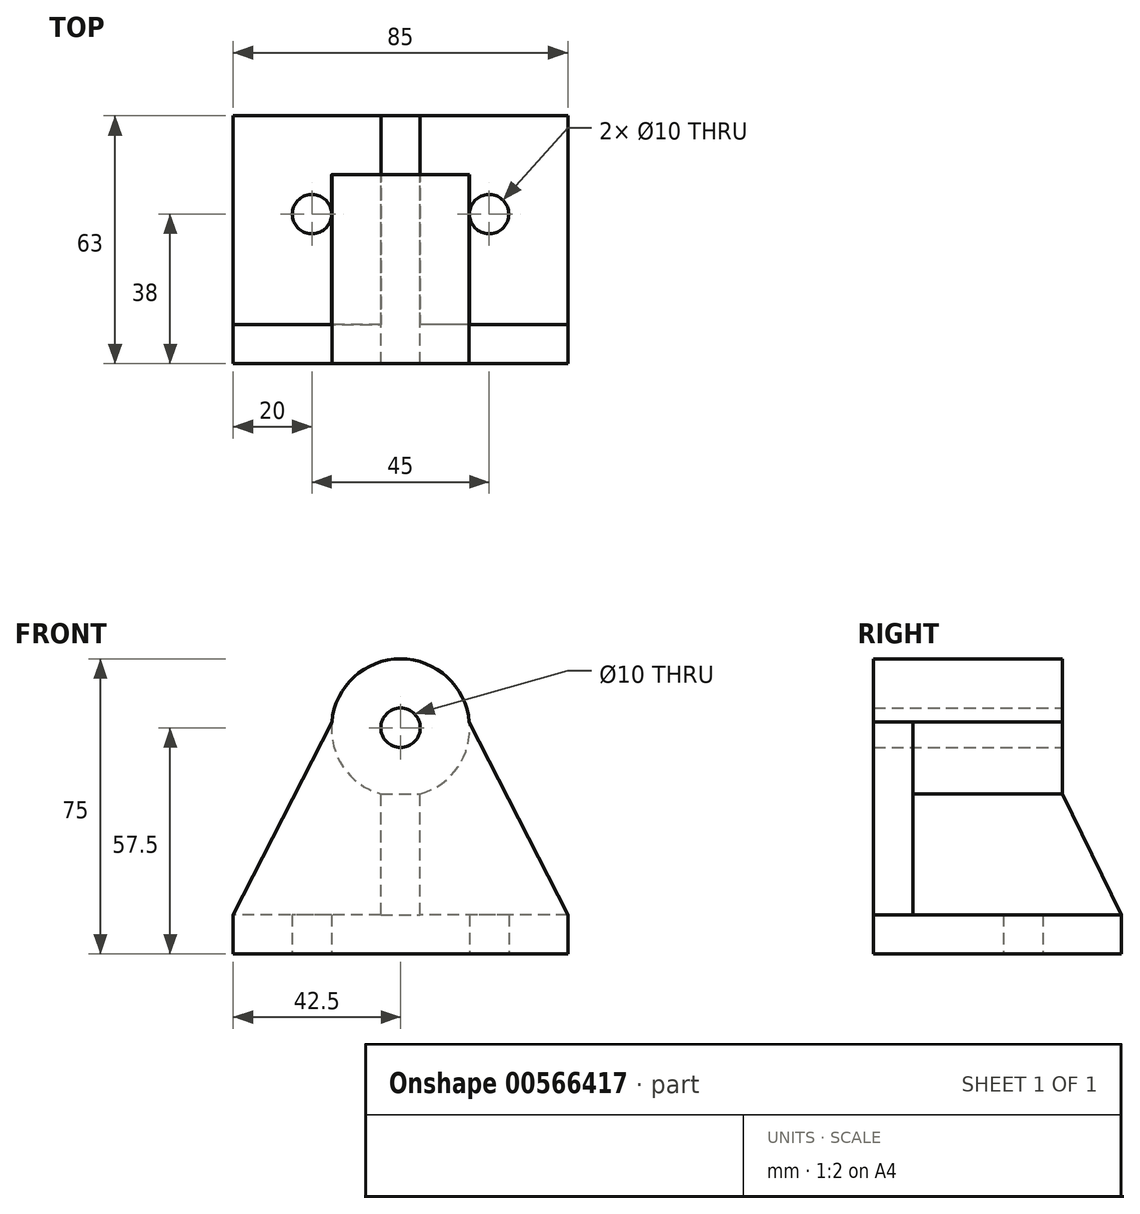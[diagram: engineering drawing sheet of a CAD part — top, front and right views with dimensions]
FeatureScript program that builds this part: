
annotation { "Feature Type Name" : "Feature", "Feature Type Description" : "" }
export const myFeature = defineFeature(function(context is Context, id is Id, definition is map)
    precondition{}
    {
        {
            var Q0;
            Q0=qCreatedBy(makeId("Front.planeOp"),FACE);
            var sketch = newSketch(context, id + "F0", { "sketchPlane" : qUnion([Q0])});
            skLineSegment(sketch, "E0", {"start": v(0, 0) * mm, "end": v(-42.5, 0) * mm});
            skLineSegment(sketch, "E1", {"start": v(-42.5, 0) * mm, "end": v(-42.5, 10) * mm});
            skCircle(sketch, "E2", {"center": v(0, 57.5) * mm, "radius": 17.5 * mm});
            skCircle(sketch, "E3", {"center": v(0, 57.5) * mm, "radius": 5 * mm});
            skLineSegment(sketch, "E4", {"start": v(0, 0) * mm, "end": v(-5, 0) * mm});
            skLineSegment(sketch, "E5", {"start": v(0, 0) * mm, "end": v(5, 0) * mm});
            skLineSegment(sketch, "E6", {"start": v(0, 0) * mm, "end": v(42.5, 0) * mm});
            skPoint(sketch, "E6.endSnap0", {"position": v(2.5, 0) * mm});
            skLineSegment(sketch, "E7", {"start": v(42.5, 0) * mm, "end": v(42.5, 10) * mm});
            skLineSegment(sketch, "E8", {"start": v(42.5, 10) * mm, "end": v(-42.5, 10) * mm});
            skLineSegment(sketch, "E9", {"start": v(17.44, 58.96) * mm, "end": v(42.5, 10) * mm});
            skLineSegment(sketch, "E10", {"start": v(-17.44, 58.96) * mm, "end": v(-42.5, 10) * mm});
            skLineSegment(sketch, "E11", {"start": v(0, 75) * mm, "end": v(0, 57.5) * mm, "construction": true});
            skLineSegment(sketch, "E12", {"start": v(-5, 0) * mm, "end": v(-5, 40.73) * mm});
            skLineSegment(sketch, "E13", {"start": v(5, 0) * mm, "end": v(5, 40.73) * mm});
            skSolve(sketch);
        }
        {
            var Q0;
            Q0 = qSketchRegion(id + "F0", true);
            extrude(context, id + "F1", {"entities" : qUnion([Q0]), "depth" : 63 * mm, "offsetDistance" : 25 * mm});
        }
        {
            var Q0;
            Q0=qCreatedBy(makeId("Top.planeOp"),FACE);
            var sketch = newSketch(context, id + "F2", { "sketchPlane" : qUnion([Q0])});
            skCircle(sketch, "E14", {"center": v(-22.5, -25) * mm, "radius": 5 * mm});
            skCircle(sketch, "E15.MirrorC", {"center": v(22.5, -25) * mm, "radius": 5 * mm});
            skSolve(sketch);
        }
        {
            var Q0;
            Q0 = qSketchRegion(id + "F2", true);
            extrude(context, id + "F3", {"entities" : qUnion([Q0]), "operationType" : NewBodyOperationType.REMOVE, "depth" : 10 * mm, "offsetDistance" : 25 * mm});
        }
        {
            var Q0;
            Q0=makeQuery(id+"F1.opExtrude","CAP_FACE",FACE,{"disambiguationData":[OSD([sQuery(id+"F0.wireOp",EDGE,"E0"),sQuery(id+"F0.wireOp",EDGE,"E1"),sQuery(id+"F0.wireOp",EDGE,"E2"),sQuery(id+"F0.wireOp",EDGE,"E3"),sQuery(id+"F0.wireOp",EDGE,"E4"),sQuery(id+"F0.wireOp",EDGE,"E6"),sQuery(id+"F0.wireOp",EDGE,"E7"),sQuery(id+"F0.wireOp",EDGE,"E8"),sQuery(id+"F0.wireOp",EDGE,"E9"),sQuery(id+"F0.wireOp",EDGE,"E10"),sQuery(id+"F0.wireOp",EDGE,"E12"),sQuery(id+"F0.wireOp",EDGE,"E13")])],"isStart":true});
            var sketch = newSketch(context, id + "F4", { "sketchPlane" : qUnion([Q0])});
            skLineSegment(sketch, "E16", {"start": v(-42.5, 10) * mm, "end": v(-5, 10) * mm});
            skLineSegment(sketch, "E17", {"start": v(-5, 10) * mm, "end": v(-5, 40.73) * mm});
            skLineSegment(sketch, "E18", {"start": v(-17.44, 58.96) * mm, "end": v(-42.5, 10) * mm});
            skArc(sketch, "E19", {"start": v(-17.44, 58.96) * mm, "mid": v(-14.58, 47.55) * mm, "end": v(-5, 40.73) * mm});
            skArc(sketch, "E20.MirrorCS", {"start": v(17.44, 58.96) * mm, "mid": v(14.58, 47.55) * mm, "end": v(5, 40.73) * mm});
            skLineSegment(sketch, "E21.MirrorCS", {"start": v(17.44, 58.96) * mm, "end": v(42.5, 10) * mm});
            skLineSegment(sketch, "E22.MirrorCS", {"start": v(5, 10) * mm, "end": v(5, 40.73) * mm});
            skLineSegment(sketch, "E23.MirrorCS", {"start": v(42.5, 10) * mm, "end": v(5, 10) * mm});
            skSolve(sketch);
        }
        {
            var Q0;
            Q0 = qSketchRegion(id + "F4", true);
            extrude(context, id + "F5", {"entities" : qUnion([Q0]), "operationType" : NewBodyOperationType.REMOVE, "oppositeDirection" : true, "depth" : 53 * mm, "offsetDistance" : 25 * mm});
        }
        {
            var Q0;
            Q0=makeQuery(id+"F1.opExtrude","CAP_FACE",FACE,{"disambiguationData":[OSD([sQuery(id+"F0.wireOp",EDGE,"E0"),sQuery(id+"F0.wireOp",EDGE,"E1"),sQuery(id+"F0.wireOp",EDGE,"E2"),sQuery(id+"F0.wireOp",EDGE,"E3"),sQuery(id+"F0.wireOp",EDGE,"E4"),sQuery(id+"F0.wireOp",EDGE,"E6"),sQuery(id+"F0.wireOp",EDGE,"E7"),sQuery(id+"F0.wireOp",EDGE,"E8"),sQuery(id+"F0.wireOp",EDGE,"E9"),sQuery(id+"F0.wireOp",EDGE,"E10"),sQuery(id+"F0.wireOp",EDGE,"E12"),sQuery(id+"F0.wireOp",EDGE,"E13")])],"isStart":false});
            var sketch = newSketch(context, id + "F6", { "sketchPlane" : qUnion([Q0])});
            skLineSegment(sketch, "E24", {"start": v(-5, 10) * mm, "end": v(5, 10) * mm});
            skLineSegment(sketch, "E25", {"start": v(5, 10) * mm, "end": v(5, 40.73) * mm});
            skLineSegment(sketch, "E26", {"start": v(-5, 10) * mm, "end": v(-5, 40.73) * mm});
            skArc(sketch, "E27", {"start": v(5, 40.73) * mm, "mid": v(0, 40) * mm, "end": v(-5, 40.73) * mm});
            skSolve(sketch);
        }
        {
            var Q0;
            Q0 = qSketchRegion(id + "F6", true);
            extrude(context, id + "F7", {"entities" : qUnion([Q0]), "operationType" : NewBodyOperationType.ADD, "oppositeDirection" : true, "depth" : 63 * mm, "offsetDistance" : 25 * mm});
        }
        {
            var Q0;
            Q0=makeQuery(id+"F7.opExtrude","SWEPT_FACE",FACE,{"disambiguationData":[OSD([sQuery(id+"F6.wireOp",EDGE,"E25")])]});
            var sketch = newSketch(context, id + "F8", { "sketchPlane" : qUnion([Q0])});
            skLineSegment(sketch, "E28", {"start": v(0, 10) * mm, "end": v(-15, 40.73) * mm});
            skLineSegment(sketch, "E29", {"start": v(-15, 75) * mm, "end": v(0, 75) * mm});
            skLineSegment(sketch, "E30", {"start": v(0, 75) * mm, "end": v(0, 10) * mm});
            skLineSegment(sketch, "E31", {"start": v(-15, 40.73) * mm, "end": v(-15, 75) * mm});
            skSolve(sketch);
        }
        {
            var Q0;
            Q0 = qSketchRegion(id + "F8", true);
            extrude(context, id + "F9", {"entities" : qUnion([Q0]), "operationType" : NewBodyOperationType.REMOVE, "endBound" : BoundingType.SYMMETRIC, "oppositeDirection" : true, "depth" : 50 * mm, "offsetDistance" : 25 * mm});
        }
    });
